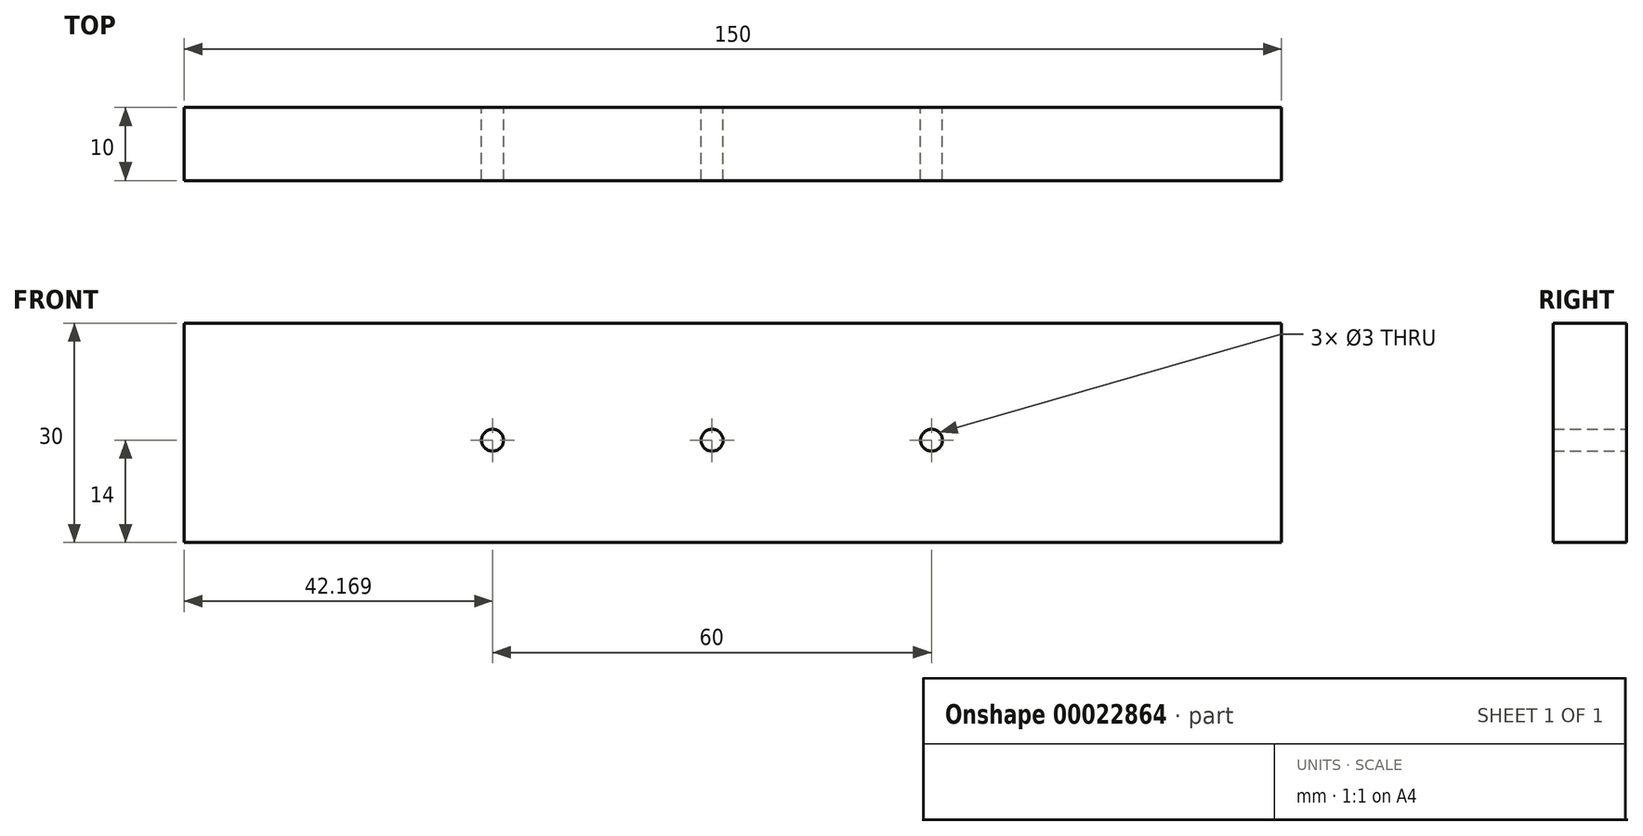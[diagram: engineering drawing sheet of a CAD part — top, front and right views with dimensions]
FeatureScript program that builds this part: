
annotation { "Feature Type Name" : "Feature", "Feature Type Description" : "" }
export const myFeature = defineFeature(function(context is Context, id is Id, definition is map)
    precondition{}
    {
        {
            var Q0;
            Q0=qCreatedBy(makeId("Front.planeOp"),FACE);
            var sketch = newSketch(context, id + "F0", { "sketchPlane" : qUnion([Q0])});
            skLineSegment(sketch, "E0.bottom", {"start": v(0, 0) * mm, "end": v(-150, 0) * mm});
            skLineSegment(sketch, "E0.top", {"start": v(0, 30) * mm, "end": v(-150, 30) * mm});
            skLineSegment(sketch, "E0.left", {"start": v(0, 0) * mm, "end": v(0, 30) * mm});
            skLineSegment(sketch, "E0.right", {"start": v(-150, 0) * mm, "end": v(-150, 30) * mm});
            skCircle(sketch, "E1", {"center": v(-77.83, 14) * mm, "radius": 1.5 * mm});
            skCircle(sketch, "E2", {"center": v(-47.83, 14) * mm, "radius": 1.5 * mm});
            skCircle(sketch, "E3", {"center": v(-107.83, 14) * mm, "radius": 1.5 * mm});
            skSolve(sketch);
        }
        {
            var Q0;
            Q0=makeQuery(id+"F0.imprint","IMPRINT",FACE,{"disambiguationData":[TD([[makeQuery(id+"F0.imprint","IMPRINT",EDGE,{"derivedFrom":sQuery(id+"F0.wireOp",EDGE,"E0.bottom")}),-1.0]])]});
            extrude(context, id + "F1", {"entities" : qUnion([Q0]), "depth" : 10 * mm});
        }
    });
